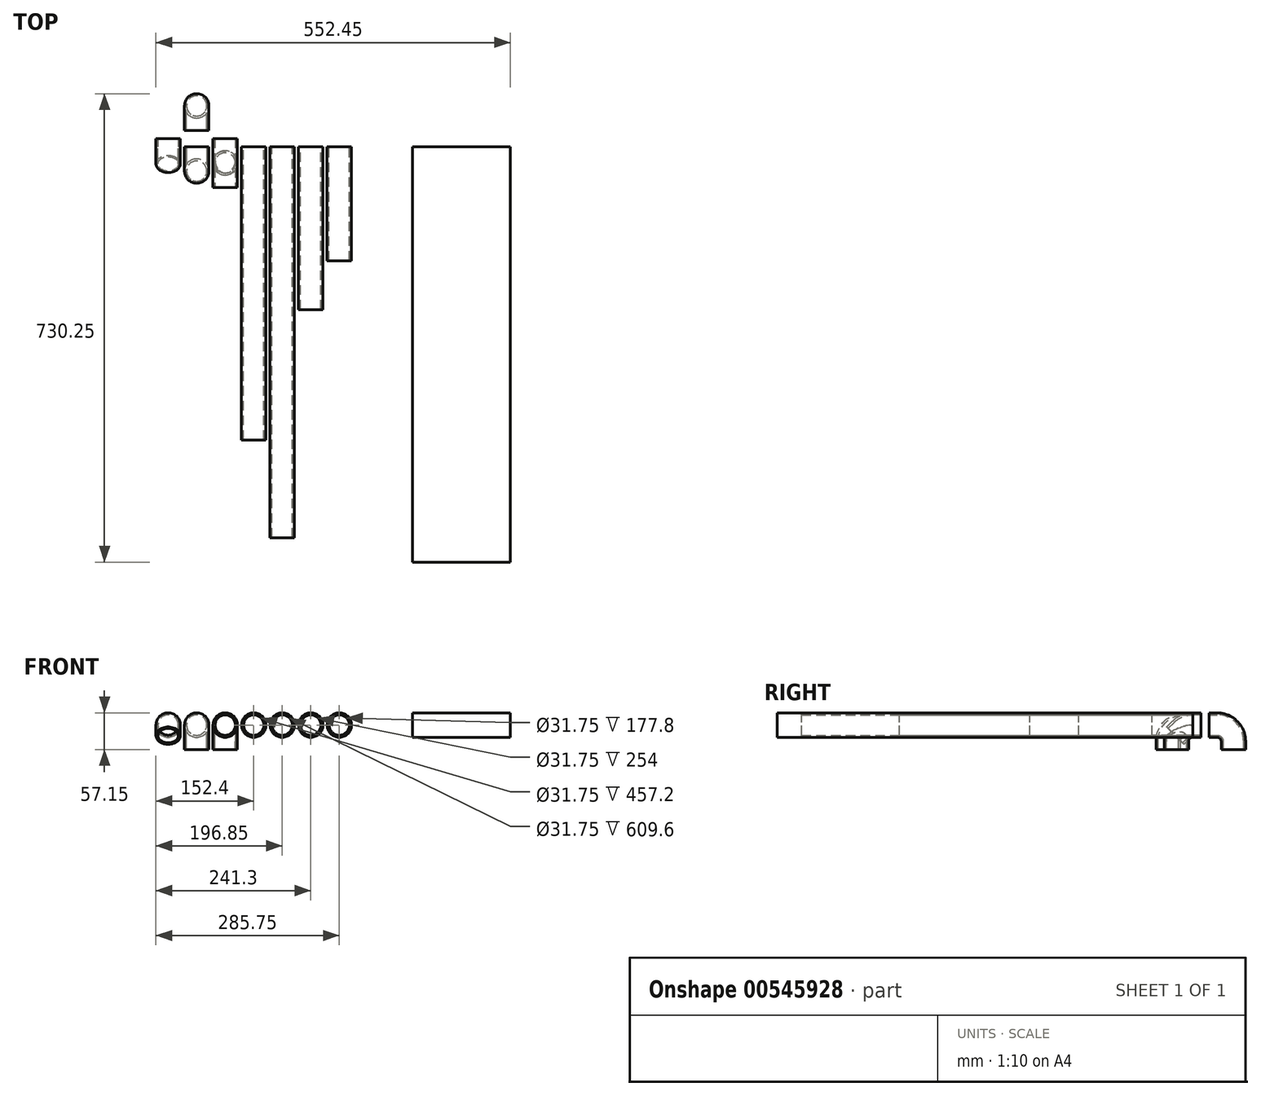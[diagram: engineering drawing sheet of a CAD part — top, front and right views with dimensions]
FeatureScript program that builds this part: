
annotation { "Feature Type Name" : "Feature", "Feature Type Description" : "" }
export const myFeature = defineFeature(function(context is Context, id is Id, definition is map)
    precondition{}
    {
        {
            var Q0;
            Q0=qCreatedBy(makeId("Front.planeOp"),FACE);
            var sketch = newSketch(context, id + "F0", { "sketchPlane" : qUnion([Q0])});
            skCircle(sketch, "E0", {"center": v(25.4, 25.4) * mm, "radius": 19.05 * mm});
            skCircle(sketch, "E1", {"center": v(25.4, 25.4) * mm, "radius": 15.88 * mm});
            skLineSegment(sketch, "E2", {"start": v(0, 0) * mm, "end": v(48.61, 0) * mm});
            skSolve(sketch);
        }
        {
            var Q0;
            Q0=qCreatedBy(makeId("Front.planeOp"),FACE);
            var sketch = newSketch(context, id + "F1", { "sketchPlane" : qUnion([Q0])});
            skCircle(sketch, "E3", {"center": v(69.85, 25.4) * mm, "radius": 19.05 * mm});
            skCircle(sketch, "E4", {"center": v(69.85, 25.4) * mm, "radius": 15.88 * mm});
            skLineSegment(sketch, "E5", {"start": v(0, 0) * mm, "end": v(75.43, 0) * mm});
            skCircle(sketch, "E6", {"center": v(158.75, 25.4) * mm, "radius": 19.05 * mm});
            skCircle(sketch, "E7", {"center": v(158.75, 25.4) * mm, "radius": 15.88 * mm});
            skCircle(sketch, "E8", {"center": v(203.2, 25.4) * mm, "radius": 19.05 * mm});
            skCircle(sketch, "E9", {"center": v(203.2, 25.4) * mm, "radius": 15.88 * mm});
            skCircle(sketch, "E10", {"center": v(247.65, 25.4) * mm, "radius": 19.05 * mm});
            skCircle(sketch, "E11", {"center": v(247.65, 25.4) * mm, "radius": 15.88 * mm});
            skCircle(sketch, "E12", {"center": v(292.1, 25.4) * mm, "radius": 19.05 * mm});
            skCircle(sketch, "E13", {"center": v(292.1, 25.4) * mm, "radius": 15.88 * mm});
            skCircle(sketch, "E14", {"center": v(336.55, 25.4) * mm, "radius": 19.05 * mm});
            skCircle(sketch, "E15", {"center": v(336.55, 25.4) * mm, "radius": 15.88 * mm});
            skLineSegment(sketch, "E16.bottom", {"start": v(406.4, 6.35) * mm, "end": v(558.8, 6.35) * mm});
            skLineSegment(sketch, "E16.top", {"start": v(406.4, 44.45) * mm, "end": v(558.8, 44.45) * mm});
            skLineSegment(sketch, "E16.left", {"start": v(406.4, 6.35) * mm, "end": v(406.4, 44.45) * mm});
            skLineSegment(sketch, "E16.right", {"start": v(558.8, 6.35) * mm, "end": v(558.8, 44.45) * mm});
            skSolve(sketch);
        }
        {
            var Q0;
            Q0=qCreatedBy(makeId("Front.planeOp"),FACE);
            var sketch = newSketch(context, id + "F2", { "sketchPlane" : qUnion([Q0])});
            skCircle(sketch, "E17", {"center": v(114.3, 25.4) * mm, "radius": 19.05 * mm});
            skCircle(sketch, "E18", {"center": v(114.3, 25.4) * mm, "radius": 15.88 * mm});
            skSolve(sketch);
        }
        {
            var Q0;
            Q0=makeQuery(id+"F0.imprint","IMPRINT",FACE,{"disambiguationData":[TD([[makeQuery(id+"F0.imprint","IMPRINT",EDGE,{"derivedFrom":sQuery(id+"F0.wireOp",EDGE,"E0")}),1.0]])]});
            var Q1;
            Q1=sQuery(id+"F0.wireOp",EDGE,"E2");
            revolve(context, id + "F3", {"entities" : qUnion([Q0]), "axis" : qUnion([Q1]), "revolveType" : RevolveType.ONE_DIRECTION, "angle" : 45 * degree});
        }
        {
            var Q0;
            Q0=makeQuery(id+"F3.opRevolve","CAP_FACE",FACE,{"disambiguationData":[OSD([sQuery(id+"F0.wireOp",EDGE,"E0"),sQuery(id+"F0.wireOp",EDGE,"E1")])],"isStart":true});
            extrude(context, id + "F4", {"entities" : qUnion([Q0]), "operationType" : NewBodyOperationType.ADD, "depth" : 12.7 * mm, "offsetDistance" : 25.4 * mm});
        }
        {
            var Q0;
            Q0=makeQuery(id+"F3.opRevolve","CAP_FACE",FACE,{"disambiguationData":[OSD([sQuery(id+"F0.wireOp",EDGE,"E0"),sQuery(id+"F0.wireOp",EDGE,"E1")])],"isStart":false});
            extrude(context, id + "F5", {"entities" : qUnion([Q0]), "operationType" : NewBodyOperationType.ADD, "depth" : 12.7 * mm, "offsetDistance" : 25.4 * mm});
        }
        {
            var Q0;
            Q0=makeQuery(id+"F1.imprint","IMPRINT",FACE,{"disambiguationData":[TD([[makeQuery(id+"F1.imprint","IMPRINT",EDGE,{"derivedFrom":sQuery(id+"F1.wireOp",EDGE,"E3")}),1.0]])]});
            var Q1;
            Q1=sQuery(id+"F1.wireOp",EDGE,"E5");
            revolve(context, id + "F6", {"entities" : qUnion([Q0]), "axis" : qUnion([Q1]), "revolveType" : RevolveType.ONE_DIRECTION, "angle" : 90 * degree});
        }
        {
            var Q0;
            Q0=makeQuery(id+"F6.opRevolve","CAP_FACE",FACE,{"disambiguationData":[OSD([sQuery(id+"F1.wireOp",EDGE,"E3"),sQuery(id+"F1.wireOp",EDGE,"E4")])],"isStart":true});
            extrude(context, id + "F7", {"entities" : qUnion([Q0]), "operationType" : NewBodyOperationType.ADD, "depth" : 12.7 * mm, "offsetDistance" : 25.4 * mm});
        }
        {
            var Q0;
            Q0=makeQuery(id+"F6.opRevolve","CAP_FACE",FACE,{"disambiguationData":[OSD([sQuery(id+"F1.wireOp",EDGE,"E3"),sQuery(id+"F1.wireOp",EDGE,"E4")])],"isStart":false});
            extrude(context, id + "F8", {"entities" : qUnion([Q0]), "operationType" : NewBodyOperationType.ADD, "depth" : 12.7 * mm, "offsetDistance" : 25.4 * mm});
        }
        {
            var Q0;
            Q0=makeQuery(id+"F6.opRevolve","SWEPT_BODY",BODY,{"disambiguationData":[OSD([sQuery(id+"F1.wireOp",EDGE,"E3"),sQuery(id+"F1.wireOp",EDGE,"E4")])]});
            transform(context, id + "F9", {"entities" : qUnion([Q0]), "transformType" : TransformType.TRANSLATION_3D, "dx" : 44.45 * mm, "dy" : 0 * mm, "dz" : 0 * mm, "makeCopy" : true});
        }
        {
            var Q0;
            Q0=makeQuery(id+"F2.imprint","IMPRINT",FACE,{"disambiguationData":[TD([[makeQuery(id+"F2.imprint","IMPRINT",EDGE,{"derivedFrom":sQuery(id+"F2.wireOp",EDGE,"E17")}),1.0]])]});
            extrude(context, id + "F10", {"entities" : qUnion([Q0]), "operationType" : NewBodyOperationType.ADD, "depth" : 63.5 * mm, "offsetDistance" : 25.4 * mm});
        }
        {
            var Q0;
            Q0=makeQuery(id+"F2.imprint","IMPRINT",FACE,{"disambiguationData":[TD([[makeQuery(id+"F2.imprint","IMPRINT",EDGE,{"derivedFrom":sQuery(id+"F2.wireOp",EDGE,"E18")}),1.0]])]});
            extrude(context, id + "F11", {"entities" : qUnion([Q0]), "operationType" : NewBodyOperationType.REMOVE, "oppositeDirection" : true, "depth" : -101.6 * mm, "offsetDistance" : 25.4 * mm});
        }
        {
            var Q0;
            Q0=makeQuery(id+"F1.imprint","IMPRINT",FACE,{"disambiguationData":[TD([[makeQuery(id+"F1.imprint","IMPRINT",EDGE,{"derivedFrom":sQuery(id+"F1.wireOp",EDGE,"E6")}),1.0]])]});
            extrude(context, id + "F12", {"entities" : qUnion([Q0]), "depth" : 457.2 * mm, "offsetDistance" : 25.4 * mm});
        }
        {
            var Q0;
            Q0=makeQuery(id+"F1.imprint","IMPRINT",FACE,{"disambiguationData":[TD([[makeQuery(id+"F1.imprint","IMPRINT",EDGE,{"derivedFrom":sQuery(id+"F1.wireOp",EDGE,"E8")}),1.0]])]});
            extrude(context, id + "F13", {"entities" : qUnion([Q0]), "depth" : 609.6 * mm, "offsetDistance" : 25.4 * mm});
        }
        {
            var Q0;
            Q0=makeQuery(id+"F6.opRevolve","SWEPT_BODY",BODY,{"disambiguationData":[OSD([sQuery(id+"F1.wireOp",EDGE,"E3"),sQuery(id+"F1.wireOp",EDGE,"E4")])]});
            transform(context, id + "F14", {"entities" : qUnion([Q0]), "transformType" : TransformType.TRANSLATION_3D, "dx" : 0 * mm, "dy" : -12.7 * mm, "dz" : 0 * mm, "makeCopy" : false});
        }
        {
            var Q0;
            Q0=makeQuery(id+"F6.opRevolve","SWEPT_BODY",BODY,{"disambiguationData":[OSD([sQuery(id+"F1.wireOp",EDGE,"E3"),sQuery(id+"F1.wireOp",EDGE,"E4")])]});
            var Q1;
            Q1=qCreatedBy(makeId("Front.planeOp"),FACE);
            mirror(context, id + "F15", {"entities" : qUnion([Q0]), "mirrorPlane" : qUnion([Q1])});
        }
        {
            var Q0;
            Q0=makeQuery(id+"F15.opPattern","COPY",BODY,{"derivedFrom":makeQuery(id+"F6.opRevolve","SWEPT_BODY",BODY,{"disambiguationData":[OSD([sQuery(id+"F1.wireOp",EDGE,"E3"),sQuery(id+"F1.wireOp",EDGE,"E4")])]}),"instanceName":"1"});
            transform(context, id + "F16", {"entities" : qUnion([Q0]), "transformType" : TransformType.TRANSLATION_3D, "dx" : 0 * mm, "dy" : 25.4 * mm, "dz" : 0 * mm, "makeCopy" : false});
        }
        {
            var Q0;
            Q0=makeQuery(id+"F1.imprint","IMPRINT",FACE,{"disambiguationData":[TD([[makeQuery(id+"F1.imprint","IMPRINT",EDGE,{"derivedFrom":sQuery(id+"F1.wireOp",EDGE,"E10")}),1.0]])]});
            extrude(context, id + "F17", {"entities" : qUnion([Q0]), "depth" : 254 * mm, "offsetDistance" : 25.4 * mm});
        }
        {
            var Q0;
            Q0=makeQuery(id+"F1.imprint","IMPRINT",FACE,{"disambiguationData":[TD([[makeQuery(id+"F1.imprint","IMPRINT",EDGE,{"derivedFrom":sQuery(id+"F1.wireOp",EDGE,"E12")}),1.0]])]});
            extrude(context, id + "F18", {"entities" : qUnion([Q0]), "depth" : 177.8 * mm, "offsetDistance" : 25.4 * mm});
        }
        {
            var Q0;
            Q0=makeQuery(id+"F1.imprint","IMPRINT",FACE,{"disambiguationData":[TD([[makeQuery(id+"F1.imprint","IMPRINT",EDGE,{"derivedFrom":sQuery(id+"F1.wireOp",EDGE,"E16.bottom")}),1.0]])]});
            extrude(context, id + "F19", {"entities" : qUnion([Q0]), "depth" : 647.7 * mm, "offsetDistance" : 25.4 * mm});
        }
    });
